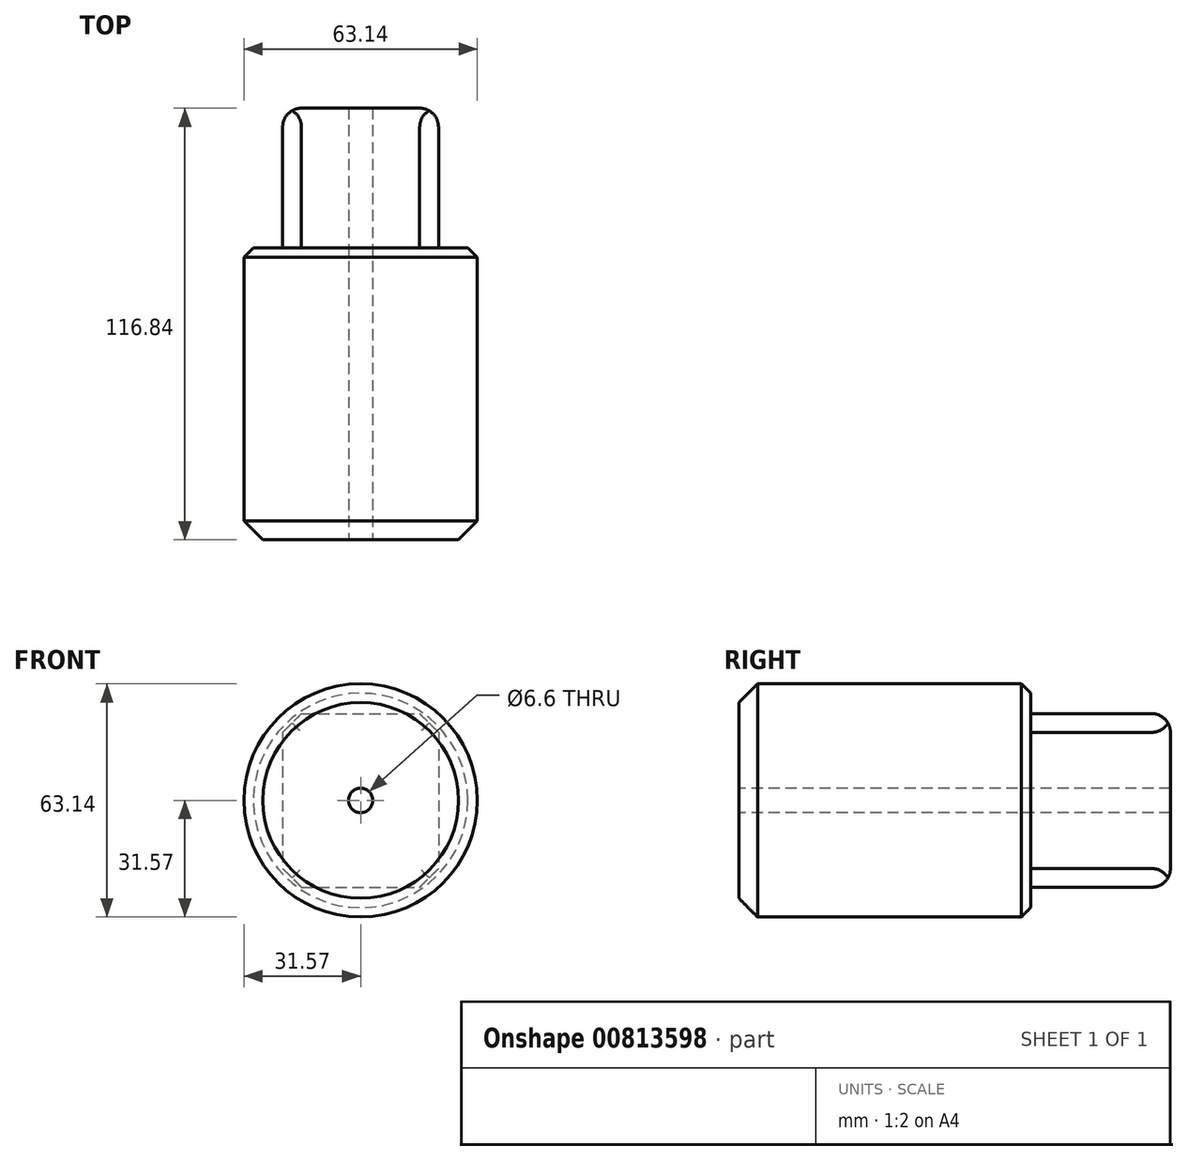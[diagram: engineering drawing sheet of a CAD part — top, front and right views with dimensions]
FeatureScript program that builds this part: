
annotation { "Feature Type Name" : "Feature", "Feature Type Description" : "" }
export const myFeature = defineFeature(function(context is Context, id is Id, definition is map)
    precondition{}
    {
        {
            var Q0;
            Q0=qCreatedBy(makeId("Front.planeOp"),FACE);
            var sketch = newSketch(context, id + "F0", { "sketchPlane" : qUnion([Q0])});
            skCircle(sketch, "E0", {"center": v(0, 0) * mm, "radius": 31.57 * mm});
            skSolve(sketch);
        }
        {
            var Q0;
            Q0=makeQuery(id+"F0.imprint","IMPRINT",FACE,{"disambiguationData":[TD([[makeQuery(id+"F0.imprint","IMPRINT",EDGE,{"derivedFrom":sQuery(id+"F0.wireOp",EDGE,"E0")}),1.0]])]});
            extrude(context, id + "F1", {"entities" : qUnion([Q0]), "depth" : 79 * mm, "offsetDistance" : 25.4 * mm});
        }
        {
            var Q0;
            Q0=makeQuery(id+"F1.opExtrude","CAP_FACE",FACE,{"disambiguationData":[OSD([sQuery(id+"F0.wireOp",EDGE,"E0")])],"isStart":false});
            var sketch = newSketch(context, id + "F2", { "sketchPlane" : qUnion([Q0])});
            skPoint(sketch, "E1", {"position": v(0, 0) * mm});
            skSolve(sketch);
        }
        {
            var Q0;
            Q0=sQuery(id+"F2.wireOp",VERTEX,"E1");
            var Q1;
            Q1=makeQuery(id+"F1.opExtrude","SWEPT_BODY",BODY,{"disambiguationData":[OSD([sQuery(id+"F0.wireOp",EDGE,"E0")])]});
            hole(context, id + "F3", {"style" : HoleStyle.SIMPLE, "endStyle" : HoleEndStyle.THROUGH, "standardTappedOrClearance" : lookupTablePath({ "standard" : "ISO", "fit" : "Normal", "size" : "M6", "type" : "Clearance" }), "standardBlindInLast" : lookupTablePath({ "fit" : "Standard", "standard" : "ISO", "size" : "M6", "type" : "Clearance" }), "holeDiameter" : 6.6 * mm, "majorDiameter" : 6.35 * mm, "isTappedThrough" : true, "tappedDepth" : 12.7 * mm, "tapClearance" : 3, "locations" : qUnion([Q0]), "scope" : qUnion([Q1])});
        }
        {
            var Q0;
            Q0=makeQuery(id+"F1.opExtrude","CAP_FACE",FACE,{"disambiguationData":[OSD([sQuery(id+"F0.wireOp",EDGE,"E0")])],"isStart":false});
            var sketch = newSketch(context, id + "F4", { "sketchPlane" : qUnion([Q0])});
            skSolve(sketch);
        }
        {
            var Q0;
            Q0=makeQuery(id+"F1.opExtrude","CAP_FACE",FACE,{"disambiguationData":[OSD([sQuery(id+"F0.wireOp",EDGE,"E0")])],"isStart":true});
            var sketch = newSketch(context, id + "F5", { "sketchPlane" : qUnion([Q0])});
            skLineSegment(sketch, "E2.bottom", {"start": v(21.08, 23.5) * mm, "end": v(-21.08, 23.5) * mm});
            skLineSegment(sketch, "E2.top", {"start": v(21.08, -23.5) * mm, "end": v(-21.08, -23.5) * mm});
            skLineSegment(sketch, "E2.left", {"start": v(21.08, 23.5) * mm, "end": v(21.08, -23.5) * mm});
            skLineSegment(sketch, "E2.right", {"start": v(-21.08, 23.5) * mm, "end": v(-21.08, -23.5) * mm});
            skSolve(sketch);
        }
        {
            var Q0;
            Q0=makeQuery(id+"F5.imprint","IMPRINT",FACE,{"disambiguationData":[TD([[makeQuery(id+"F5.imprint","IMPRINT",EDGE,{"derivedFrom":sQuery(id+"F5.wireOp",EDGE,"E2.bottom")}),1.0]])]});
            extrude(context, id + "F6", {"entities" : qUnion([Q0]), "operationType" : NewBodyOperationType.ADD, "depth" : 37.85 * mm, "offsetDistance" : 25.4 * mm});
        }
        {
            var Q0;
            Q0=makeQuery(id+"F6.opExtrude","SWEPT_EDGE",EDGE,{"disambiguationData":[OSD([sQuery(id+"F0.wireOp",EDGE,"E0"),sQuery(id+"F5.wireOp",EDGE,"E2.bottom"),sQuery(id+"F5.wireOp",EDGE,"E2.right")])]});
            var Q1;
            Q1=makeQuery(id+"F6.opExtrude","SWEPT_EDGE",EDGE,{"disambiguationData":[OSD([sQuery(id+"F0.wireOp",EDGE,"E0"),sQuery(id+"F5.wireOp",EDGE,"E2.top"),sQuery(id+"F5.wireOp",EDGE,"E2.right")])]});
            var Q2;
            Q2=makeQuery(id+"F6.opExtrude","SWEPT_EDGE",EDGE,{"disambiguationData":[OSD([sQuery(id+"F0.wireOp",EDGE,"E0"),sQuery(id+"F5.wireOp",EDGE,"E2.bottom"),sQuery(id+"F5.wireOp",EDGE,"E2.left")])]});
            var Q3;
            Q3=makeQuery(id+"F6.opExtrude","SWEPT_EDGE",EDGE,{"disambiguationData":[OSD([sQuery(id+"F0.wireOp",EDGE,"E0"),sQuery(id+"F5.wireOp",EDGE,"E2.top"),sQuery(id+"F5.wireOp",EDGE,"E2.left")])]});
            chamfer(context, id + "F7", {"entities" : qUnion([Q0, Q1, Q2, Q3]), "chamferType" : ChamferType.OFFSET_ANGLE, "width" : 5.08 * mm, "oppositeDirection" : false, "angle" : 45 * degree, "tangentPropagation" : true});
        }
        {
            var Q0;
            Q0=makeQuery(id+"F6.opExtrude","CAP_EDGE",EDGE,{"disambiguationData":[OSD([sQuery(id+"F5.wireOp",EDGE,"E2.top")])],"isStart":false});
            var Q1;
            Q1=makeQuery(id+"F6.opExtrude","CAP_EDGE",EDGE,{"disambiguationData":[OSD([sQuery(id+"F5.wireOp",EDGE,"E2.right")])],"isStart":false});
            var Q2;
            Q2=makeQuery(id+"F6.opExtrude","CAP_EDGE",EDGE,{"disambiguationData":[OSD([sQuery(id+"F5.wireOp",EDGE,"E2.bottom")])],"isStart":false});
            var Q3;
            Q3=makeQuery(id+"F6.opExtrude","CAP_EDGE",EDGE,{"disambiguationData":[OSD([sQuery(id+"F5.wireOp",EDGE,"E2.left")])],"isStart":false});
            fillet(context, id + "F8", {"entities" : qUnion([Q0, Q1, Q2, Q3]), "radius" : 5.08 * mm, "tangentPropagation" : true, "allowEdgeOverflow" : false});
        }
        {
            var Q0;
            {var subQ0=sQuery(id+"F0.wireOp",EDGE,"E0");Q0=makeQuery(id+"F6.boolean.opBoolean","SPLIT",EDGE,{"disambiguationData":[TD([makeQuery(id+"F1.opExtrude","SWEPT_FACE",FACE,{"disambiguationData":[OSD([subQ0])]}),makeQuery(id+"F1.opExtrude","CAP_FACE",FACE,{"disambiguationData":[OSD([subQ0])],"isStart":true}),makeQuery(id+"F6.opExtrude","SWEPT_FACE",FACE,{"disambiguationData":[OSD([sQuery(id+"F5.wireOp",EDGE,"E2.bottom")])]}),makeQuery(id+"F6.opExtrude","SWEPT_FACE",FACE,{"disambiguationData":[OSD([sQuery(id+"F5.wireOp",EDGE,"E2.top")])]}),makeQuery(id+"F6.opExtrude","SWEPT_FACE",FACE,{"disambiguationData":[OSD([sQuery(id+"F5.wireOp",EDGE,"E2.right")])]})])],"derivedFrom":makeQuery(id+"F1.opExtrude","CAP_EDGE",EDGE,{"disambiguationData":[OSD([subQ0])],"isStart":true})});}
            chamfer(context, id + "F9", {"entities" : qUnion([Q0]), "width" : 2.54 * mm, "tangentPropagation" : true});
        }
        {
            var Q0;
            Q0=makeQuery(id+"F1.opExtrude","CAP_EDGE",EDGE,{"disambiguationData":[OSD([sQuery(id+"F0.wireOp",EDGE,"E0")])],"isStart":false});
            chamfer(context, id + "F10", {"entities" : qUnion([Q0]), "width" : 5.08 * mm, "tangentPropagation" : true});
        }
    });
